# Revit family: Shower-Handshower_Kit-KOHLER-STANCE-K-72844T_1
name_source: partatom
category: Plumbing Fixtures
units: mm (PartAtom-declared; Revit-internal decimal feet)

## family parameters
Cut with Voids When Loaded = No
Host = Face
Maintain Annotation Orientation = No
OmniClass Number = 23.31.17.00
OmniClass Title = Showers
Part Type = Normal
Room Calculation Point = No
Round Connector Dimension = Use Diameter
Shared = No

## types (3) — shared parameters
ADA Compliant = No
Assembly Code = D2010700
CW Connection = Yes
Cold Water Inlet = Cold Water Inlet
Date Modified = 04/21/2022
Default Elevation = 36"
Description = Wall-Mounted Bath Shower Faucet (Ingenious)
Drain Included = No
Flow Rate = 10 GPM
HW Connection = Yes
Handle Clearance = 1 5/16"
Height = 19 5/16"
Hot Water Inlet = Hot Water Inlet
Length = 9 5/8"
Manufacturer = KOHLER Co.
Master Format 2014 = 22 42 23
Master Format 2014 Name = Residential Showers
Material = Premium Metal Construction
Pressure = 45.00 psi
Product Documentation Link = https://files.kohler.com.cn
Product Name = Stance
Spout Reach = 4 13/16"
URL = http://www.kohler.com.cn
Vent Connection = No
Waste Connection = No
Waste Water Outlet = Waste Water Outlet
WaterSense Certified = No
Width = 11 1/16"

## per-type parameters (varying)
| type | Finish | Model | Product Page URL | Secondary Finish | Type |
| CP-Polished Chrome | Kohler-Metal-CP-Polished_Chrome | K-72844T-9-CP | https://www.kohler.com.cn | Kohler-Plastic-0-White | 1 |
| 2BL-Original Black | Kohler-Metal-2BL-Original_Black | K-72844T-9-2BL | https://www.kohler.com.cn | Kohler-Plastic-58-Thunder_Grey | 2 |
| BL-Matte Black | Kohler-Metal-BL-Matte_Black | K-72844T-9-BL |  | Kohler-Plastic-58-Thunder_Grey | 3 |

## geometry (parser evidence)
native form markers: Sweep x6
no freeform markers — native parametric forms only
